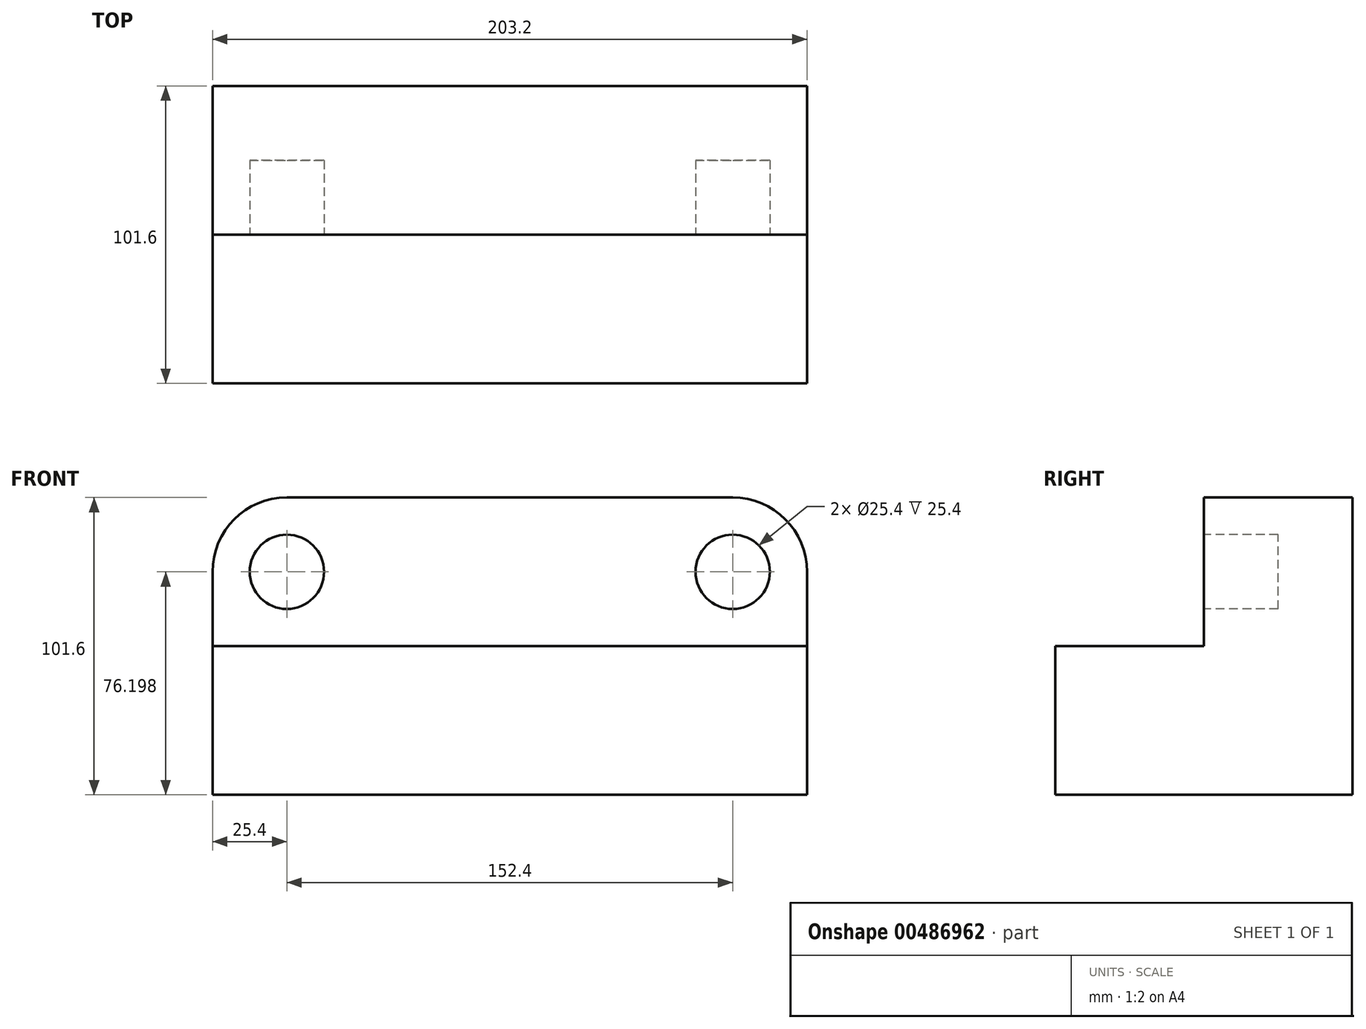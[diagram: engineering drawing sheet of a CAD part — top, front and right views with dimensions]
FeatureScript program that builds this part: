
annotation { "Feature Type Name" : "Feature", "Feature Type Description" : "" }
export const myFeature = defineFeature(function(context is Context, id is Id, definition is map)
    precondition{}
    {
        {
            var Q0;
            Q0=qCreatedBy(makeId("Right.planeOp"),FACE);
            var sketch = newSketch(context, id + "F0", { "sketchPlane" : qUnion([Q0])});
            skLineSegment(sketch, "E0.bottom", {"start": v(-36, 3.18) * mm, "end": v(14.8, 3.18) * mm});
            skLineSegment(sketch, "E0.top", {"start": v(-36, -47.62) * mm, "end": v(65.6, -47.62) * mm});
            skLineSegment(sketch, "E0.left", {"start": v(-36, 3.18) * mm, "end": v(-36, -47.62) * mm});
            skLineSegment(sketch, "E0.right", {"start": v(65.6, 3.18) * mm, "end": v(65.6, -47.62) * mm});
            skLineSegment(sketch, "E1.top", {"start": v(65.6, 53.98) * mm, "end": v(14.8, 53.98) * mm});
            skLineSegment(sketch, "E1.left", {"start": v(65.6, 3.18) * mm, "end": v(65.6, 53.98) * mm});
            skLineSegment(sketch, "E1.right", {"start": v(14.8, 3.18) * mm, "end": v(14.8, 53.98) * mm});
            skSolve(sketch);
        }
        {
            var Q0;
            Q0 = qSketchRegion(id + "F0", true);
            extrude(context, id + "F1", {"entities" : qUnion([Q0]), "depth" : 203.2 * mm});
        }
        {
            var Q0;
            Q0=makeQuery(id+"F1.opExtrude","SWEPT_FACE",FACE,{"disambiguationData":[OSD([sQuery(id+"F0.wireOp",EDGE,"E0.top")])]});
            var sketch = newSketch(context, id + "F2", { "sketchPlane" : qUnion([Q0])});
            skLineSegment(sketch, "E2.bottom", {"start": v(0, 36) * mm, "end": v(76.2, 36) * mm});
            skLineSegment(sketch, "E2.top", {"start": v(0, 86.8) * mm, "end": v(76.2, 86.8) * mm});
            skLineSegment(sketch, "E2.left", {"start": v(0, 36) * mm, "end": v(0, 86.8) * mm});
            skLineSegment(sketch, "E2.right", {"start": v(76.2, 36) * mm, "end": v(76.2, 86.8) * mm});
            skLineSegment(sketch, "E3.bottom", {"start": v(203.2, 36) * mm, "end": v(279.4, 36) * mm});
            skLineSegment(sketch, "E3.top", {"start": v(203.2, -14.8) * mm, "end": v(279.4, -14.8) * mm});
            skLineSegment(sketch, "E3.left", {"start": v(203.2, 36) * mm, "end": v(203.2, -14.8) * mm});
            skLineSegment(sketch, "E3.right", {"start": v(279.4, 36) * mm, "end": v(279.4, -14.8) * mm});
            skSolve(sketch);
        }
        {
            var Q0;
            Q0 = qSketchRegion(id + "F2", true);
            extrude(context, id + "F3", {"entities" : qUnion([Q0]), "operationType" : NewBodyOperationType.REMOVE, "oppositeDirection" : true, "depth" : 50.8 * mm});
        }
        {
            var Q0;
            Q0=makeQuery(id+"F1.opExtrude","CAP_EDGE",EDGE,{"disambiguationData":[OSD([sQuery(id+"F0.wireOp",EDGE,"E1.top")])],"isStart":true});
            var Q1;
            Q1=makeQuery(id+"F1.opExtrude","CAP_EDGE",EDGE,{"disambiguationData":[OSD([sQuery(id+"F0.wireOp",EDGE,"E1.top")])],"isStart":false});
            fillet(context, id + "F4", {"entities" : qUnion([Q0, Q1]), "radius" : 25.4 * mm, "tangentPropagation" : true, "allowEdgeOverflow" : false});
        }
        {
            var Q0;
            Q0=makeQuery(id+"F1.opExtrude","SWEPT_FACE",FACE,{"disambiguationData":[OSD([sQuery(id+"F0.wireOp",EDGE,"E1.right")])]});
            var sketch = newSketch(context, id + "F5", { "sketchPlane" : qUnion([Q0])});
            skCircle(sketch, "E4", {"center": v(25.4, 28.58) * mm, "radius": 12.7 * mm});
            skCircle(sketch, "E5", {"center": v(177.8, 28.58) * mm, "radius": 12.7 * mm});
            skSolve(sketch);
        }
        {
            var Q0;
            Q0 = qSketchRegion(id + "F5", true);
            extrude(context, id + "F6", {"entities" : qUnion([Q0]), "operationType" : NewBodyOperationType.REMOVE, "oppositeDirection" : true, "depth" : 25.4 * mm});
        }
    });
